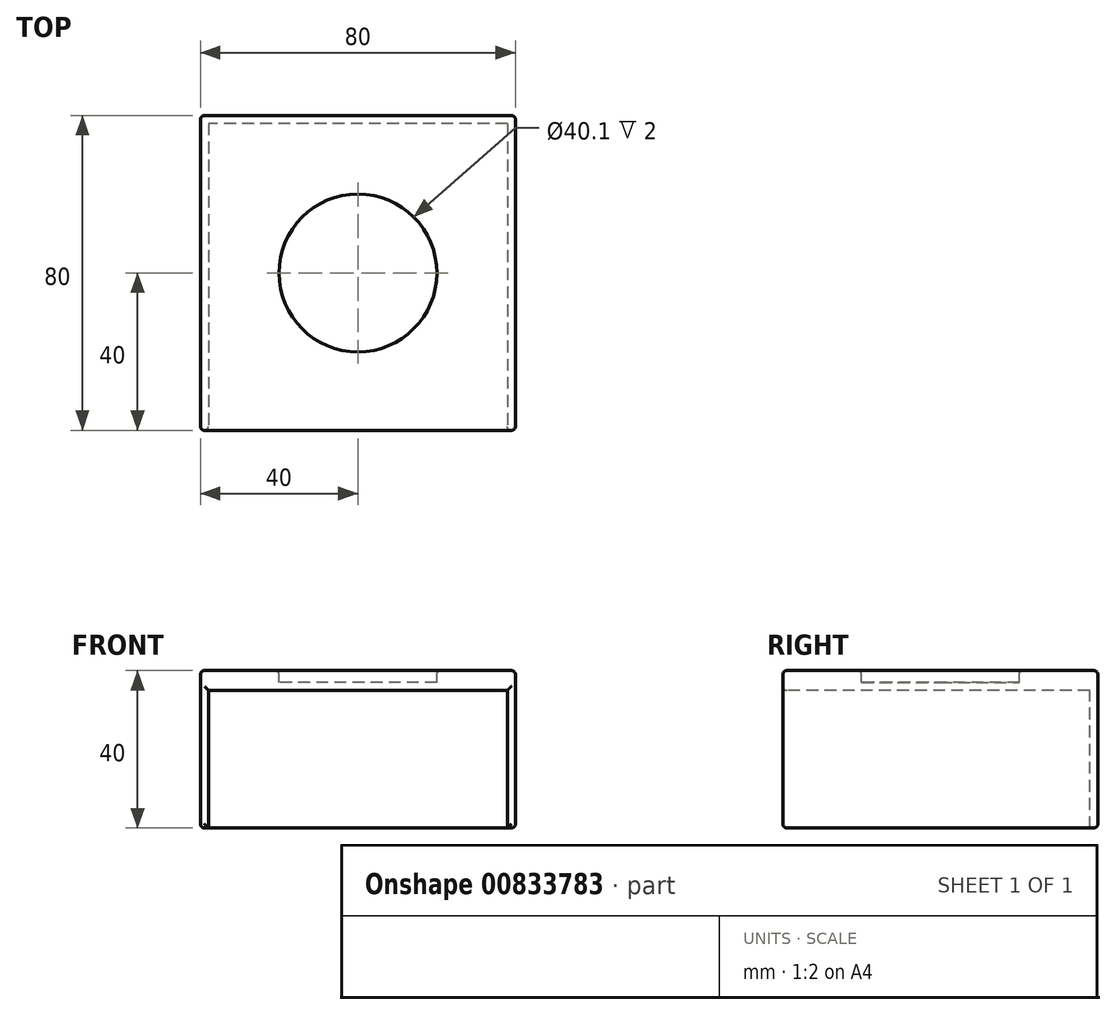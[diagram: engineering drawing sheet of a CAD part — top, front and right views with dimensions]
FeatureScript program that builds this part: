
annotation { "Feature Type Name" : "Feature", "Feature Type Description" : "" }
export const myFeature = defineFeature(function(context is Context, id is Id, definition is map)
    precondition{}
    {
        {
            var Q0;
            Q0=qCreatedBy(makeId("Front.planeOp"),FACE);
            var sketch = newSketch(context, id + "F0", { "sketchPlane" : qUnion([Q0])});
            skLineSegment(sketch, "E0.bottom", {"start": v(40, -20) * mm, "end": v(-40, -20) * mm});
            skLineSegment(sketch, "E0.top", {"start": v(40, 20) * mm, "end": v(-40, 20) * mm});
            skLineSegment(sketch, "E0.left", {"start": v(40, -20) * mm, "end": v(40, 20) * mm});
            skLineSegment(sketch, "E0.right", {"start": v(-40, -20) * mm, "end": v(-40, 20) * mm});
            skPoint(sketch, "E0.middle", {"position": v(0, 0) * mm});
            skSolve(sketch);
        }
        {
            var Q0;
            Q0 = qSketchRegion(id + "F0", true);
            extrude(context, id + "F1", {"entities" : qUnion([Q0]), "depth" : 40 * mm, "offsetDistance" : 25 * mm, "hasSecondDirection" : true, "secondDirectionOppositeDirection" : true, "secondDirectionDepth" : 40 * mm});
        }
        {
            var Q0;
            Q0=makeQuery(id+"F1.opExtrude","CAP_FACE",FACE,{"disambiguationData":[OSD([sQuery(id+"F0.wireOp",EDGE,"E0.bottom"),sQuery(id+"F0.wireOp",EDGE,"E0.top"),sQuery(id+"F0.wireOp",EDGE,"E0.left"),sQuery(id+"F0.wireOp",EDGE,"E0.right")])],"isStart":false});
            var sketch = newSketch(context, id + "F2", { "sketchPlane" : qUnion([Q0])});
            skLineSegment(sketch, "E1.bottom", {"start": v(-38, -20) * mm, "end": v(38, -20) * mm});
            skLineSegment(sketch, "E1.top", {"start": v(-38, 15) * mm, "end": v(38, 15) * mm});
            skLineSegment(sketch, "E1.left", {"start": v(-38, -20) * mm, "end": v(-38, 15) * mm});
            skLineSegment(sketch, "E1.right", {"start": v(38, -20) * mm, "end": v(38, 15) * mm});
            skSolve(sketch);
        }
        {
            var Q0;
            Q0 = qSketchRegion(id + "F2", true);
            extrude(context, id + "F3", {"entities" : qUnion([Q0]), "operationType" : NewBodyOperationType.REMOVE, "oppositeDirection" : true, "depth" : 78 * mm, "offsetDistance" : 25 * mm});
        }
        {
            var Q0;
            Q0=makeQuery(id+"F1.opExtrude","SWEPT_FACE",FACE,{"disambiguationData":[OSD([sQuery(id+"F0.wireOp",EDGE,"E0.top")])]});
            var sketch = newSketch(context, id + "F4", { "sketchPlane" : qUnion([Q0])});
            skCircle(sketch, "E2", {"center": v(0, 0) * mm, "radius": 20.05 * mm});
            skSolve(sketch);
        }
        {
            var Q0;
            Q0 = qSketchRegion(id + "F4", true);
            extrude(context, id + "F5", {"entities" : qUnion([Q0]), "operationType" : NewBodyOperationType.REMOVE, "oppositeDirection" : true, "depth" : 3 * mm, "offsetDistance" : 25 * mm});
        }
        {
            var Q0;
            Q0=makeQuery(id+"F1.opExtrude","SWEPT_FACE",FACE,{"disambiguationData":[OSD([sQuery(id+"F0.wireOp",EDGE,"E0.left")])]});
            var Q1;
            Q1=makeQuery(id+"F1.opExtrude","CAP_FACE",FACE,{"disambiguationData":[OSD([sQuery(id+"F0.wireOp",EDGE,"E0.bottom"),sQuery(id+"F0.wireOp",EDGE,"E0.top"),sQuery(id+"F0.wireOp",EDGE,"E0.left"),sQuery(id+"F0.wireOp",EDGE,"E0.right")])],"isStart":false});
            var Q2;
            Q2=makeQuery(id+"F1.opExtrude","SWEPT_FACE",FACE,{"disambiguationData":[OSD([sQuery(id+"F0.wireOp",EDGE,"E0.top")])]});
            var Q3;
            Q3=makeQuery(id+"F1.opExtrude","CAP_FACE",FACE,{"disambiguationData":[OSD([sQuery(id+"F0.wireOp",EDGE,"E0.bottom"),sQuery(id+"F0.wireOp",EDGE,"E0.top"),sQuery(id+"F0.wireOp",EDGE,"E0.left"),sQuery(id+"F0.wireOp",EDGE,"E0.right")])],"isStart":true});
            var Q4;
            Q4=makeQuery(id+"F1.opExtrude","SWEPT_FACE",FACE,{"disambiguationData":[OSD([sQuery(id+"F0.wireOp",EDGE,"E0.right")])]});
            fillet(context, id + "F6", {"entities" : qUnion([Q0, Q1, Q2, Q3, Q4]), "tangentPropagation" : true, "radius" : 1 * mm, "defaultsChanged" : false, "vertexSettings" : [], "allowEdgeOverflow" : false});
        }
    });
